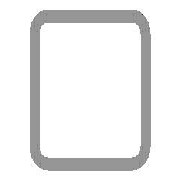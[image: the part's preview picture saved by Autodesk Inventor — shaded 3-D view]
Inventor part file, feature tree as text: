
AUTODESK INVENTOR PART (.ipt)
format: ipt  version: 2022 (Build 260153000, 153)  size: 178,688 bytes
history: native  units: mm (DEFAULTED — no unit token found)
features: other x5, sketch x2, sweep x1, plane x1
ambient origin geometry x8: Origin, YZ Plane, XZ Plane, XY Plane, X Axis, Y Axis, Z Axis, Center Point
bodies: Solid1 (feature_tree), Body (feature_tree)
feature tree (9):
  parser-record x1  (decoder bookkeeping rows leaked as tree rows — omitted from the tree; the rows remain in map.json)
  other  "Driven Length"
  other  "Start Plane"
  other  "End Plane"
  sweep  "Sweep Path"
  other  "Orientation Work Plane"
  sketch  "Sketch3"  dims[d7=7.5mm d10=40.0mm]
  plane  "Work Plane3"
  sketch  "Sketch4"  dims[d11=40.0mm d12=5.0mm d13=-0.0mm d14=3875.406592mm d15=20.0mm d16=20.0mm d17=90.0deg d18=3875.406592mm d19=0.0mm d20=0.0mm]
